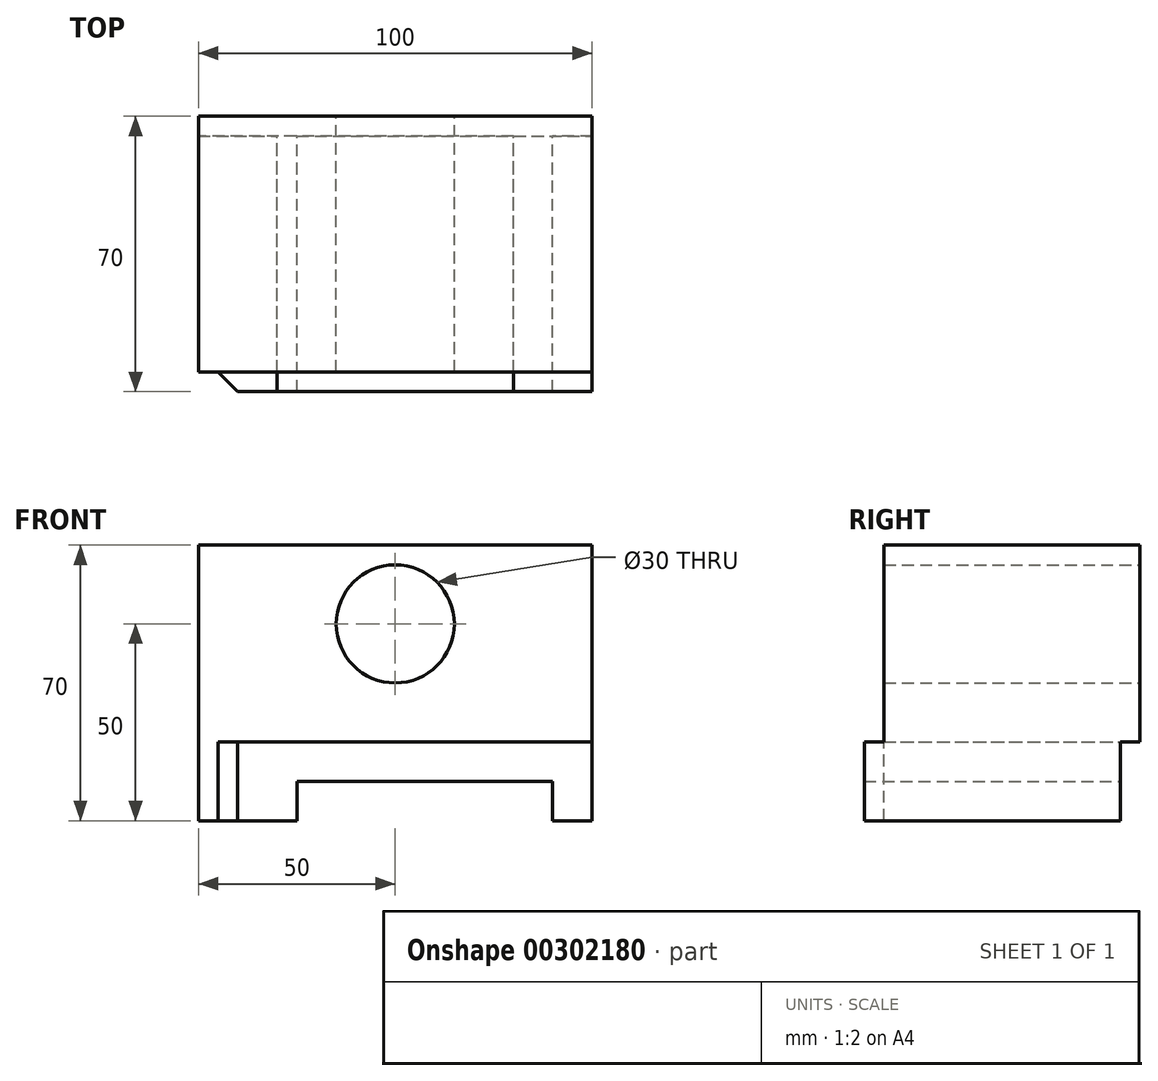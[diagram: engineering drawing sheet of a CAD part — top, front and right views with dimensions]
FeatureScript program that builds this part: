
annotation { "Feature Type Name" : "Feature", "Feature Type Description" : "" }
export const myFeature = defineFeature(function(context is Context, id is Id, definition is map)
    precondition{}
    {
        {
            var Q0;
            Q0=qCreatedBy(makeId("Front.planeOp"),FACE);
            var sketch = newSketch(context, id + "F0", { "sketchPlane" : qUnion([Q0])});
            skLineSegment(sketch, "E0.bottom", {"start": v(50, -35) * mm, "end": v(-50, -35) * mm});
            skLineSegment(sketch, "E0.top", {"start": v(50, 35) * mm, "end": v(-50, 35) * mm});
            skLineSegment(sketch, "E0.left", {"start": v(50, -35) * mm, "end": v(50, 35) * mm});
            skLineSegment(sketch, "E0.right", {"start": v(-50, -35) * mm, "end": v(-50, 35) * mm});
            skPoint(sketch, "E0.middle", {"position": v(0, 0) * mm});
            skLineSegment(sketch, "E1.bottom", {"start": v(30, -15) * mm, "end": v(-30, -15) * mm});
            skLineSegment(sketch, "E1.top", {"start": v(30, 15) * mm, "end": v(-30, 15) * mm});
            skLineSegment(sketch, "E1.left", {"start": v(30, -15) * mm, "end": v(30, 15) * mm});
            skLineSegment(sketch, "E1.right", {"start": v(-30, -15) * mm, "end": v(-30, 15) * mm});
            skLineSegment(sketch, "E2.bottom", {"start": v(-25, -35) * mm, "end": v(40, -35) * mm});
            skLineSegment(sketch, "E2.top", {"start": v(-25, -25) * mm, "end": v(40, -25) * mm});
            skLineSegment(sketch, "E2.left", {"start": v(-25, -35) * mm, "end": v(-25, -25) * mm});
            skLineSegment(sketch, "E2.right", {"start": v(40, -35) * mm, "end": v(40, -25) * mm});
            skCircle(sketch, "E3", {"center": v(0, 15) * mm, "radius": 15 * mm});
            skCircle(sketch, "E4", {"center": v(0, 15) * mm, "radius": 10 * mm});
            skLineSegment(sketch, "E5", {"start": v(-50, -14.93) * mm, "end": v(50, -15) * mm});
            skSolve(sketch);
        }
        {
            var Q0;
            {var subQ3=sQuery(id+"F0.wireOp",EDGE,"E1.bottom");Q0=makeQuery(id+"F0.imprint","IMPRINT",FACE,{"disambiguationData":[TD([[makeQuery(id+"F0.imprint","IMPRINT",EDGE,{"derivedFrom":subQ3}),1.0]])]});}
            extrude(context, id + "F1", {"entities" : qUnion([Q0]), "depth" : 65 * mm});
        }
        {
            var Q0;
            {var subQ1=sQuery(id+"F0.wireOp",EDGE,"E1.top");var subQ5=sQuery(id+"F0.wireOp",EDGE,"E1.left");var subQ6=makeQuery(id+"F0.imprint","INTERSECT",VERTEX,{"derivedFrom":[subQ1,subQ5]});Q0=makeQuery(id+"F0.imprint","IMPRINT",FACE,{"disambiguationData":[TD([[makeQuery(id+"F0.imprint","IMPRINT",EDGE,{"disambiguationData":[TD([[subQ6,-1.0]])],"derivedFrom":subQ1}),1.0]])]});}
            extrude(context, id + "F2", {"entities" : qUnion([Q0]), "depth" : 45 * mm});
        }
        {
            var Q0;
            {var subQ0=sQuery(id+"F0.wireOp",EDGE,"E3");var subQ1=sQuery(id+"F0.wireOp",EDGE,"E1.top");var subQ2=makeQuery(id+"F0.imprint","INTERSECT",VERTEX,{"disambiguationData":[OD(0.0)],"derivedFrom":[subQ1,subQ0]});Q0=makeQuery(id+"F0.imprint","IMPRINT",FACE,{"disambiguationData":[TD([[makeQuery(id+"F0.imprint","IMPRINT",EDGE,{"disambiguationData":[TD([[subQ2,-1.0]])],"derivedFrom":subQ1}),1.0]])]});}
            var Q1;
            {var subQ0=sQuery(id+"F0.wireOp",EDGE,"E3");var subQ1=sQuery(id+"F0.wireOp",EDGE,"E1.top");var subQ2=makeQuery(id+"F0.imprint","INTERSECT",VERTEX,{"disambiguationData":[OD(0.0)],"derivedFrom":[subQ1,subQ0]});Q1=makeQuery(id+"F0.imprint","IMPRINT",FACE,{"disambiguationData":[TD([[makeQuery(id+"F0.imprint","IMPRINT",EDGE,{"disambiguationData":[TD([[subQ2,-1.0]])],"derivedFrom":subQ1}),-1.0]])]});}
            extrude(context, id + "F3", {"entities" : qUnion([Q0, Q1]), "operationType" : NewBodyOperationType.ADD, "depth" : 60 * mm});
        }
        {
            var Q0;
            {var subQ0=sQuery(id+"F0.wireOp",EDGE,"E5");Q0=makeQuery(id+"F1.opExtrude","SWEPT_FACE",FACE,{"disambiguationData":[OSD([subQ0]),TDD([makeQuery(id+"F0.imprint","IMPRINT",EDGE,{"disambiguationData":[TD([[makeQuery(id+"F0.imprint","INTERSECT",VERTEX,{"derivedFrom":[sQuery(id+"F0.wireOp",EDGE,"E0.right"),subQ0]}),-1.0]])],"derivedFrom":subQ0})])]});}
            var sketch = newSketch(context, id + "F4", { "sketchPlane" : qUnion([Q0])});
            skLineSegment(sketch, "E6", {"start": v(-49.99, -55) * mm, "end": v(-39.99, -65) * mm});
            skSolve(sketch);
        }
        {
            var Q0;
            {var subQ0=sQuery(id+"F4.wireOp",EDGE,"E6");Q0=makeQuery(id+"F4.imprint","IMPRINT",FACE,{"disambiguationData":[TD([[makeQuery(id+"F4.imprint","IMPRINT",EDGE,{"derivedFrom":subQ0}),-1.0]])]});}
            extrude(context, id + "F5", {"entities" : qUnion([Q0]), "operationType" : NewBodyOperationType.REMOVE, "oppositeDirection" : true, "depth" : 25 * mm});
        }
        {
            var Q0;
            {var subQ0=sQuery(id+"F0.wireOp",EDGE,"E3");var subQ1=sQuery(id+"F0.wireOp",EDGE,"E1.top");var subQ2=makeQuery(id+"F0.imprint","INTERSECT",VERTEX,{"disambiguationData":[OD(0.0)],"derivedFrom":[subQ1,subQ0]});Q0=makeQuery(id+"F0.imprint","IMPRINT",FACE,{"disambiguationData":[TD([[makeQuery(id+"F0.imprint","IMPRINT",EDGE,{"disambiguationData":[TD([[subQ2,-1.0]])],"derivedFrom":subQ1}),-1.0]])]});}
            var Q1;
            {var subQ0=sQuery(id+"F0.wireOp",EDGE,"E3");var subQ1=sQuery(id+"F0.wireOp",EDGE,"E1.top");var subQ2=makeQuery(id+"F0.imprint","INTERSECT",VERTEX,{"disambiguationData":[OD(0.0)],"derivedFrom":[subQ1,subQ0]});Q1=makeQuery(id+"F0.imprint","IMPRINT",FACE,{"disambiguationData":[TD([[makeQuery(id+"F0.imprint","IMPRINT",EDGE,{"disambiguationData":[TD([[subQ2,-1.0]])],"derivedFrom":subQ1}),1.0]])]});}
            extrude(context, id + "F6", {"entities" : qUnion([Q0, Q1]), "operationType" : NewBodyOperationType.ADD, "oppositeDirection" : true, "depth" : 5 * mm});
        }
        {
            var Q0;
            {var subQ1=sQuery(id+"F0.wireOp",EDGE,"E1.top");var subQ5=sQuery(id+"F0.wireOp",EDGE,"E1.left");var subQ6=makeQuery(id+"F0.imprint","INTERSECT",VERTEX,{"derivedFrom":[subQ1,subQ5]});Q0=makeQuery(id+"F0.imprint","IMPRINT",FACE,{"disambiguationData":[TD([[makeQuery(id+"F0.imprint","IMPRINT",EDGE,{"disambiguationData":[TD([[subQ6,-1.0]])],"derivedFrom":subQ1}),1.0]])]});}
            extrude(context, id + "F7", {"entities" : qUnion([Q0]), "operationType" : NewBodyOperationType.ADD, "depth" : 5 * mm});
        }
    });
